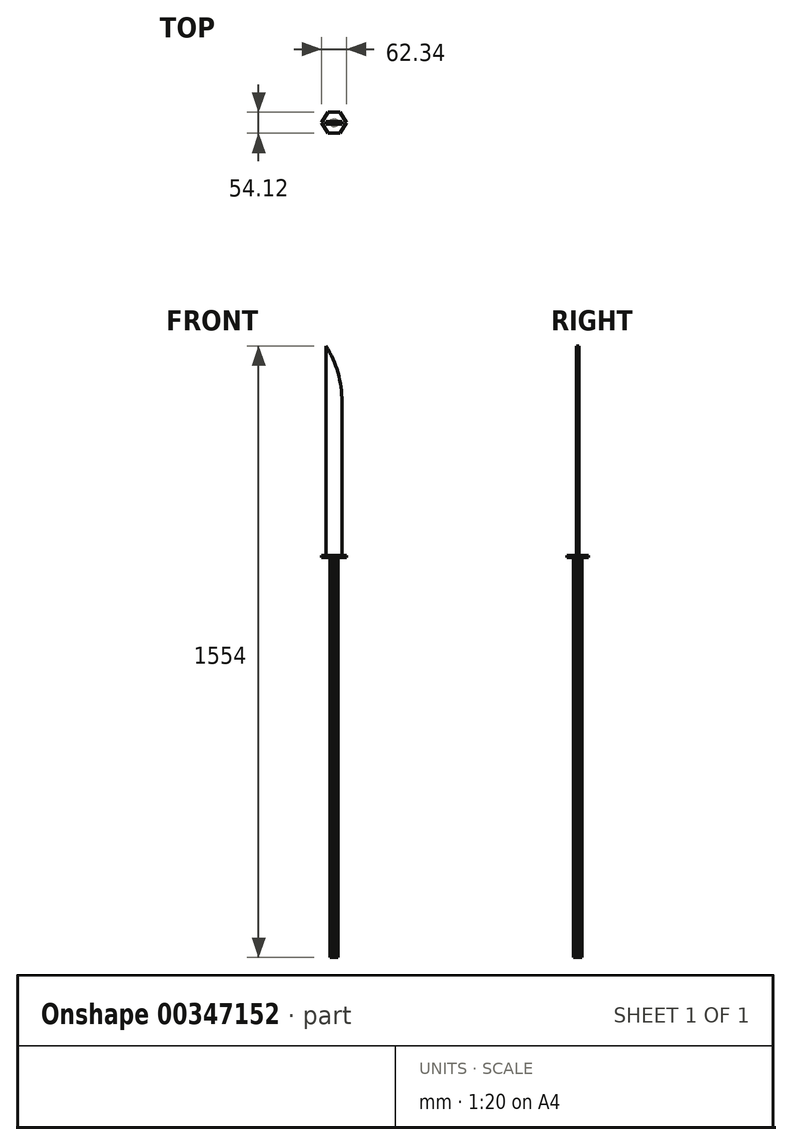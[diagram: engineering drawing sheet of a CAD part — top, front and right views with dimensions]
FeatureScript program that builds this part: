
annotation { "Feature Type Name" : "Feature", "Feature Type Description" : "" }
export const myFeature = defineFeature(function(context is Context, id is Id, definition is map)
    precondition{}
    {
        {
            var Q0;
            Q0=qCreatedBy(makeId("Top.planeOp"),FACE);
            var sketch = newSketch(context, id + "F0", { "sketchPlane" : qUnion([Q0])});
            skLineSegment(sketch, "E0.bottom", {"start": v(56.92, 4.85) * mm, "end": v(-56.92, 4.85) * mm});
            skLineSegment(sketch, "E0.top", {"start": v(56.92, -4.85) * mm, "end": v(-56.92, -4.85) * mm});
            skLineSegment(sketch, "E0.left", {"start": v(56.92, 4.85) * mm, "end": v(56.92, -4.85) * mm});
            skLineSegment(sketch, "E0.right", {"start": v(-56.92, 4.85) * mm, "end": v(-56.92, -4.85) * mm});
            skPoint(sketch, "E0.middle", {"position": v(0, 0) * mm});
            skLineSegment(sketch, "E1.bottom", {"start": v(20.15, -2.99) * mm, "end": v(-20.15, -2.99) * mm});
            skLineSegment(sketch, "E1.top", {"start": v(20.15, 2.99) * mm, "end": v(-20.15, 2.99) * mm});
            skLineSegment(sketch, "E1.left", {"start": v(20.15, -2.99) * mm, "end": v(20.15, 2.99) * mm});
            skLineSegment(sketch, "E1.right", {"start": v(-20.15, -2.99) * mm, "end": v(-20.15, 2.99) * mm});
            skSolve(sketch);
        }
        {
            var Q0;
            Q0=makeQuery(id+"F0.imprint","IMPRINT",FACE,{"disambiguationData":[TD([[makeQuery(id+"F0.imprint","IMPRINT",EDGE,{"derivedFrom":sQuery(id+"F0.wireOp",EDGE,"E1.bottom")}),-1.0]])]});
            extrude(context, id + "F1", {"entities" : qUnion([Q0]), "depth" : 537 * mm});
        }
        {
            var Q0;
            Q0=qCreatedBy(makeId("Top.planeOp"),FACE);
            var sketch = newSketch(context, id + "F2", { "sketchPlane" : qUnion([Q0])});
            skCircle(sketch, "E2.cCircle", {"center": v(0, 0) * mm, "radius": 9.86 * mm, "construction": true});
            skLineSegment(sketch, "E2.0", {"start": v(10.6, -1.3) * mm, "end": v(6.57, -8.4) * mm});
            skLineSegment(sketch, "E2.1", {"start": v(6.57, -8.4) * mm, "end": v(-1.3, -10.6) * mm});
            skLineSegment(sketch, "E2.2", {"start": v(-1.3, -10.6) * mm, "end": v(-8.4, -6.57) * mm});
            skLineSegment(sketch, "E2.3", {"start": v(-8.4, -6.57) * mm, "end": v(-10.6, 1.3) * mm});
            skLineSegment(sketch, "E2.4", {"start": v(-10.6, 1.3) * mm, "end": v(-6.57, 8.4) * mm});
            skLineSegment(sketch, "E2.5", {"start": v(-6.57, 8.4) * mm, "end": v(1.3, 10.6) * mm});
            skLineSegment(sketch, "E2.6", {"start": v(1.3, 10.6) * mm, "end": v(8.4, 6.57) * mm});
            skLineSegment(sketch, "E2.7", {"start": v(8.4, 6.57) * mm, "end": v(10.6, -1.3) * mm});
            skPoint(sketch, "E2.0.midPoint", {"position": v(8.58, -4.85) * mm});
            skSolve(sketch);
        }
        {
            var Q0;
            Q0=makeQuery(id+"F2.imprint","IMPRINT",FACE,{"disambiguationData":[TD([[makeQuery(id+"F2.imprint","IMPRINT",EDGE,{"derivedFrom":sQuery(id+"F2.wireOp",EDGE,"E2.0")}),-1.0]])]});
            extrude(context, id + "F3", {"entities" : qUnion([Q0]), "operationType" : NewBodyOperationType.ADD, "oppositeDirection" : true, "depth" : 1017 * mm});
        }
        {
            var Q0;
            Q0=qCreatedBy(makeId("Top.planeOp"),FACE);
            var sketch = newSketch(context, id + "F4", { "sketchPlane" : qUnion([Q0])});
            skCircle(sketch, "E3.cCircle", {"center": v(0, 0) * mm, "radius": 27 * mm, "construction": true});
            skLineSegment(sketch, "E3.0", {"start": v(15.7, 26.93) * mm, "end": v(31.17, -0.14) * mm});
            skLineSegment(sketch, "E3.1", {"start": v(31.17, -0.14) * mm, "end": v(15.47, -27.06) * mm});
            skLineSegment(sketch, "E3.2", {"start": v(15.47, -27.06) * mm, "end": v(-15.7, -26.93) * mm});
            skLineSegment(sketch, "E3.3", {"start": v(-15.7, -26.93) * mm, "end": v(-31.17, 0.14) * mm});
            skLineSegment(sketch, "E3.4", {"start": v(-31.17, 0.14) * mm, "end": v(-15.47, 27.06) * mm});
            skLineSegment(sketch, "E3.5", {"start": v(-15.47, 27.06) * mm, "end": v(15.7, 26.93) * mm});
            skPoint(sketch, "E3.0.midPoint", {"position": v(23.44, 13.4) * mm});
            skSolve(sketch);
        }
        {
            var Q0;
            Q0=makeQuery(id+"F4.imprint","IMPRINT",FACE,{"disambiguationData":[TD([[makeQuery(id+"F4.imprint","IMPRINT",EDGE,{"derivedFrom":sQuery(id+"F4.wireOp",EDGE,"E3.0")}),-1.0]])]});
            extrude(context, id + "F5", {"entities" : qUnion([Q0]), "operationType" : NewBodyOperationType.ADD, "depth" : 5 * mm});
        }
        {
            var Q0;
            Q0=makeQuery(id+"F1.opExtrude","CAP_EDGE",EDGE,{"disambiguationData":[OSD([sQuery(id+"F0.wireOp",EDGE,"E1.left")])],"isStart":false});
            fillet(context, id + "F6", {"entities" : qUnion([Q0]), "radius" : 270.4 * mm, "tangentPropagation" : true, "allowEdgeOverflow" : false});
        }
    });
